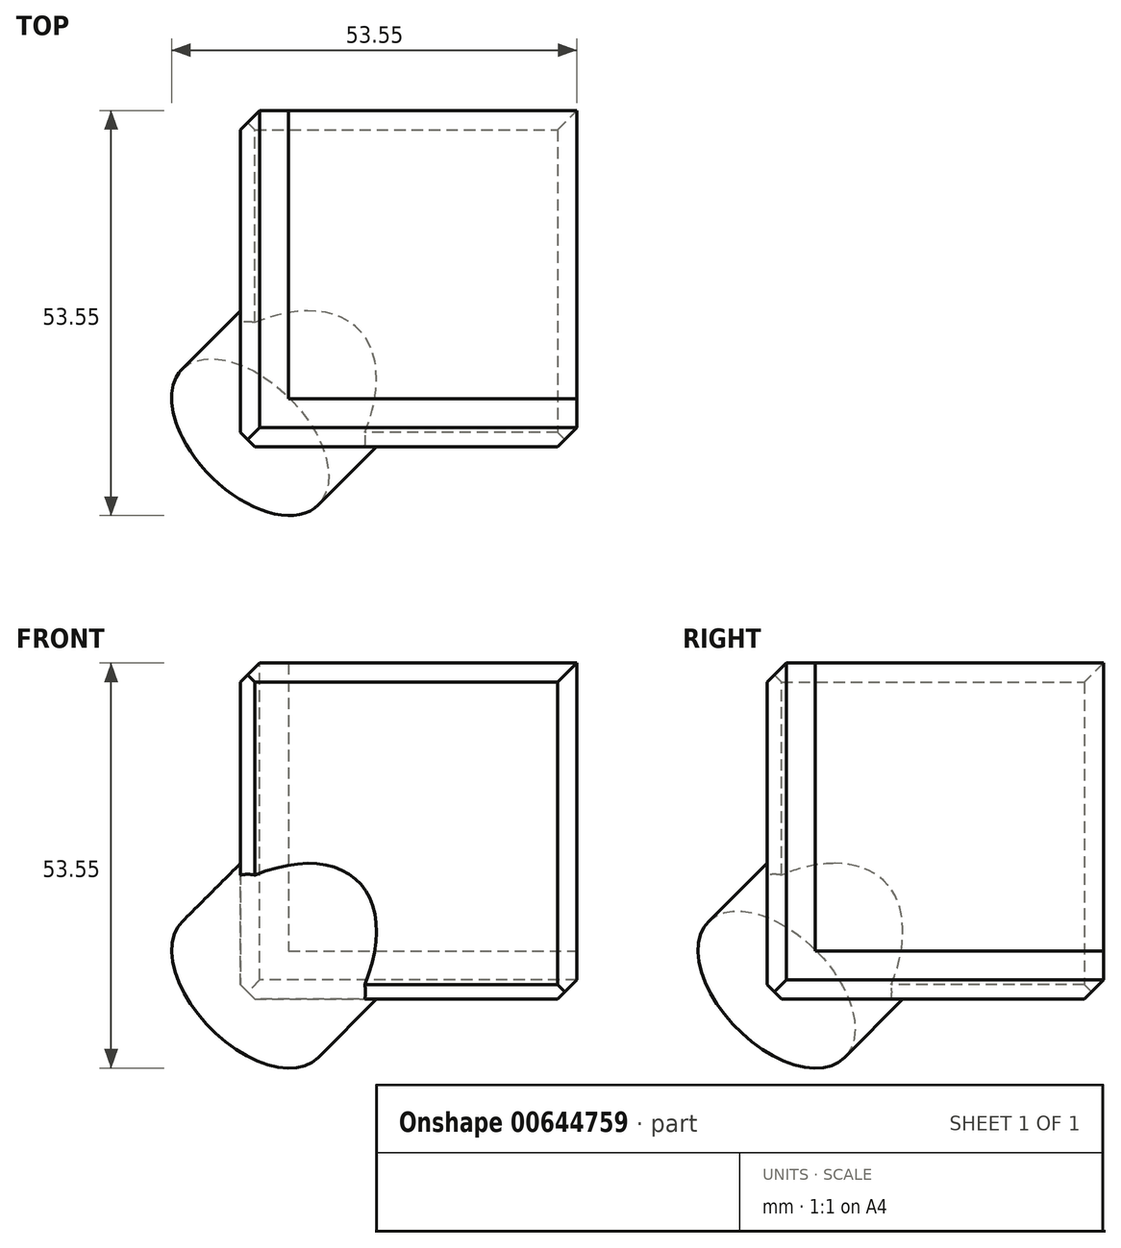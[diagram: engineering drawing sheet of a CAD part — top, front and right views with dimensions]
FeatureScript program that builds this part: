
annotation { "Feature Type Name" : "Feature", "Feature Type Description" : "" }
export const myFeature = defineFeature(function(context is Context, id is Id, definition is map)
    precondition{}
    {
        {
            var Q0;
            Q0=qCreatedBy(makeId("Top.planeOp"),FACE);
            var sketch = newSketch(context, id + "F0", { "sketchPlane" : qUnion([Q0])});
            skLineSegment(sketch, "E0.bottom", {"start": v(-20.24, 21.46) * mm, "end": v(24.2, 21.46) * mm});
            skLineSegment(sketch, "E0.top", {"start": v(-20.24, -22.99) * mm, "end": v(24.2, -22.99) * mm});
            skLineSegment(sketch, "E0.left", {"start": v(-20.24, 21.46) * mm, "end": v(-20.24, -22.99) * mm});
            skLineSegment(sketch, "E0.right", {"start": v(24.2, 21.46) * mm, "end": v(24.2, -22.99) * mm});
            skSolve(sketch);
        }
        {
            var Q0;
            Q0 = qSketchRegion(id + "F0", true);
            extrude(context, id + "F1", {"entities" : qUnion([Q0]), "depth" : 44.45 * mm, "offsetDistance" : 25.4 * mm});
        }
        {
            var Q0;
            Q0=makeQuery(id+"F1.opExtrude","SWEPT_EDGE",EDGE,{"disambiguationData":[OSD([sQuery(id+"F0.wireOp",EDGE,"E0.top"),sQuery(id+"F0.wireOp",EDGE,"E0.left")])]});
            var Q1;
            Q1=makeQuery(id+"F1.opExtrude","CAP_EDGE",EDGE,{"disambiguationData":[OSD([sQuery(id+"F0.wireOp",EDGE,"E0.top")])],"isStart":true});
            var Q2;
            Q2=makeQuery(id+"F1.opExtrude","CAP_EDGE",EDGE,{"disambiguationData":[OSD([sQuery(id+"F0.wireOp",EDGE,"E0.left")])],"isStart":true});
            chamfer(context, id + "F2", {"entities" : qUnion([Q0, Q1, Q2]), "width" : 1.9 * mm, "tangentPropagation" : true});
        }
        {
            var Q0;
            {var subQ0=sQuery(id+"F0.wireOp",EDGE,"E0.left");var subQ1=sQuery(id+"F0.wireOp",EDGE,"E0.top");Q0=makeQuery(id+"F2.opChamfer","BLEND_FACE",FACE,{"disambiguationData":[OSD([subQ1,subQ0]),TDD([makeQuery(id+"F1.opExtrude","CAP_VERTEX",VERTEX,{"disambiguationData":[OSD([subQ1,subQ0])],"isStart":true})])]});}
            var sketch = newSketch(context, id + "F3", { "sketchPlane" : qUnion([Q0])});
            skLineSegment(sketch, "E1", {"start": v(-7.53, 16.93) * mm, "end": v(-6.36, 14.9) * mm});
            skLineSegment(sketch, "E2", {"start": v(-6.36, 14.9) * mm, "end": v(-7.53, 15.58) * mm, "construction": true});
            skLineSegment(sketch, "E3", {"start": v(-7.53, 15.58) * mm, "end": v(-6.36, 17.6) * mm});
            skLineSegment(sketch, "E4", {"start": v(-6.36, 17.6) * mm, "end": v(-8.7, 16.26) * mm, "construction": true});
            skLineSegment(sketch, "E5", {"start": v(-8.7, 16.26) * mm, "end": v(-6.36, 16.26) * mm});
            skPoint(sketch, "E6", {"position": v(-7.14, 16.26) * mm});
            skCircle(sketch, "E7", {"center": v(-7.14, 16.26) * mm, "radius": 12.7 * mm});
            skSolve(sketch);
        }
        {
            var Q0;
            Q0=makeQuery(id+"F3.imprint","IMPRINT",FACE,{"disambiguationData":[TD([[makeQuery(id+"F3.imprint","IMPRINT",EDGE,{"derivedFrom":sQuery(id+"F3.wireOp",EDGE,"E7")}),1.0]])]});
            var Q1;
            {var subQ0=sQuery(id+"F3.wireOp",EDGE,"E1");var subQ6=sQuery(id+"F3.wireOp",EDGE,"E5");var subQ7=makeQuery(id+"F3.imprint","INTERSECT",VERTEX,{"derivedFrom":[subQ0,sQuery(id+"F3.wireOp",EDGE,"E3"),subQ6]});Q1=makeQuery(id+"F3.imprint","IMPRINT",FACE,{"disambiguationData":[TD([[makeQuery(id+"F3.imprint","IMPRINT",EDGE,{"disambiguationData":[TD([[subQ7,1.0]])],"derivedFrom":subQ0}),-1.0]])]});}
            var Q2;
            {var subQ0=sQuery(id+"F3.wireOp",EDGE,"E3");var subQ6=sQuery(id+"F3.wireOp",EDGE,"E5");var subQ7=makeQuery(id+"F3.imprint","INTERSECT",VERTEX,{"derivedFrom":[sQuery(id+"F3.wireOp",EDGE,"E1"),subQ0,subQ6]});Q2=makeQuery(id+"F3.imprint","IMPRINT",FACE,{"disambiguationData":[TD([[makeQuery(id+"F3.imprint","IMPRINT",EDGE,{"disambiguationData":[TD([[subQ7,1.0]])],"derivedFrom":subQ0}),1.0]])]});}
            var Q3;
            {var subQ0=sQuery(id+"F3.wireOp",EDGE,"E1");var subQ6=sQuery(id+"F3.wireOp",EDGE,"E3");var subQ7=makeQuery(id+"F3.imprint","INTERSECT",VERTEX,{"derivedFrom":[subQ0,subQ6,sQuery(id+"F3.wireOp",EDGE,"E5")]});Q3=makeQuery(id+"F3.imprint","IMPRINT",FACE,{"disambiguationData":[TD([[makeQuery(id+"F3.imprint","IMPRINT",EDGE,{"disambiguationData":[TD([[subQ7,1.0]])],"derivedFrom":subQ6}),-1.0]])]});}
            var Q4;
            {var subQ0=sQuery(id+"F3.wireOp",EDGE,"E1");var subQ6=sQuery(id+"F3.wireOp",EDGE,"E5");var subQ7=makeQuery(id+"F3.imprint","INTERSECT",VERTEX,{"derivedFrom":[subQ0,sQuery(id+"F3.wireOp",EDGE,"E3"),subQ6]});Q4=makeQuery(id+"F3.imprint","IMPRINT",FACE,{"disambiguationData":[TD([[makeQuery(id+"F3.imprint","IMPRINT",EDGE,{"disambiguationData":[TD([[subQ7,-1.0]])],"derivedFrom":subQ6}),-1.0]])]});}
            var Q5;
            {var subQ0=sQuery(id+"F3.wireOp",EDGE,"E3");var subQ6=sQuery(id+"F3.wireOp",EDGE,"E5");var subQ7=makeQuery(id+"F3.imprint","INTERSECT",VERTEX,{"derivedFrom":[sQuery(id+"F3.wireOp",EDGE,"E1"),subQ0,subQ6]});Q5=makeQuery(id+"F3.imprint","IMPRINT",FACE,{"disambiguationData":[TD([[makeQuery(id+"F3.imprint","IMPRINT",EDGE,{"disambiguationData":[TD([[subQ7,-1.0]])],"derivedFrom":subQ6}),1.0]])]});}
            var Q6;
            {var subQ0=sQuery(id+"F3.wireOp",EDGE,"E1");var subQ6=sQuery(id+"F3.wireOp",EDGE,"E3");var subQ7=makeQuery(id+"F3.imprint","INTERSECT",VERTEX,{"derivedFrom":[subQ0,subQ6,sQuery(id+"F3.wireOp",EDGE,"E5")]});Q6=makeQuery(id+"F3.imprint","IMPRINT",FACE,{"disambiguationData":[TD([[makeQuery(id+"F3.imprint","IMPRINT",EDGE,{"disambiguationData":[TD([[subQ7,1.0]])],"derivedFrom":subQ0}),1.0]])]});}
            var Q7;
            Q7=makeQuery(id+"F1.opExtrude","CAP_FACE",FACE,{"disambiguationData":[OSD([sQuery(id+"F0.wireOp",EDGE,"E0.bottom"),sQuery(id+"F0.wireOp",EDGE,"E0.top"),sQuery(id+"F0.wireOp",EDGE,"E0.left"),sQuery(id+"F0.wireOp",EDGE,"E0.right")])],"isStart":true});
            extrude(context, id + "F4", {"entities" : qUnion([Q0, Q1, Q2, Q3, Q4, Q5, Q6]), "operationType" : NewBodyOperationType.ADD, "oppositeDirection" : true, "depth" : 25.4 * mm, "endBoundEntityFace" : qUnion([Q7]), "offsetDistance" : 25.4 * mm});
        }
        {
            var Q0;
            Q0=makeQuery(id+"F1.opExtrude","SWEPT_FACE",FACE,{"disambiguationData":[OSD([sQuery(id+"F0.wireOp",EDGE,"E0.right")])]});
            var sketch = newSketch(context, id + "F5", { "sketchPlane" : qUnion([Q0])});
            skLineSegment(sketch, "E8.bottom", {"start": v(21.46, 44.45) * mm, "end": v(-16.64, 44.45) * mm});
            skLineSegment(sketch, "E8.top", {"start": v(21.46, 6.35) * mm, "end": v(-16.64, 6.35) * mm});
            skLineSegment(sketch, "E8.left", {"start": v(21.46, 44.45) * mm, "end": v(21.46, 6.35) * mm});
            skLineSegment(sketch, "E8.right", {"start": v(-16.64, 44.45) * mm, "end": v(-16.64, 6.35) * mm});
            skSolve(sketch);
        }
        {
            var Q0;
            Q0=makeQuery(id+"F5.imprint","IMPRINT",FACE,{"disambiguationData":[TD([[makeQuery(id+"F5.imprint","IMPRINT",EDGE,{"derivedFrom":sQuery(id+"F5.wireOp",EDGE,"E8.bottom")}),1.0]])]});
            extrude(context, id + "F6", {"entities" : qUnion([Q0]), "operationType" : NewBodyOperationType.REMOVE, "oppositeDirection" : true, "depth" : 38.1 * mm, "offsetDistance" : 25.4 * mm});
        }
        {
            var Q0;
            Q0=makeQuery(id+"F1.opExtrude","SWEPT_EDGE",EDGE,{"disambiguationData":[OSD([sQuery(id+"F0.wireOp",EDGE,"E0.bottom"),sQuery(id+"F0.wireOp",EDGE,"E0.left")])]});
            var Q1;
            Q1=makeQuery(id+"F1.opExtrude","CAP_EDGE",EDGE,{"disambiguationData":[OSD([sQuery(id+"F0.wireOp",EDGE,"E0.bottom")])],"isStart":true});
            var Q2;
            Q2=makeQuery(id+"F1.opExtrude","CAP_EDGE",EDGE,{"disambiguationData":[OSD([sQuery(id+"F0.wireOp",EDGE,"E0.top")])],"isStart":false});
            var Q3;
            Q3=makeQuery(id+"F1.opExtrude","CAP_EDGE",EDGE,{"disambiguationData":[OSD([sQuery(id+"F0.wireOp",EDGE,"E0.left")])],"isStart":false});
            var Q4;
            Q4=makeQuery(id+"F1.opExtrude","SWEPT_EDGE",EDGE,{"disambiguationData":[OSD([sQuery(id+"F0.wireOp",EDGE,"E0.top"),sQuery(id+"F0.wireOp",EDGE,"E0.right")])]});
            var Q5;
            Q5=makeQuery(id+"F1.opExtrude","CAP_EDGE",EDGE,{"disambiguationData":[OSD([sQuery(id+"F0.wireOp",EDGE,"E0.right")])],"isStart":true});
            var Q6;
            Q6=makeQuery(id+"F6.boolean.opBoolean","COPY",EDGE,{"derivedFrom":makeQuery(id+"F6.opExtrude","SWEPT_EDGE",EDGE,{"disambiguationData":[OSD([sQuery(id+"F0.wireOp",EDGE,"E0.bottom"),sQuery(id+"F0.wireOp",EDGE,"E0.right"),sQuery(id+"F5.wireOp",EDGE,"E8.top"),sQuery(id+"F5.wireOp",EDGE,"E8.left")])]})});
            var Q7;
            Q7=makeQuery(id+"F6.boolean.opBoolean","COPY",EDGE,{"derivedFrom":makeQuery(id+"F6.opExtrude","CAP_EDGE",EDGE,{"disambiguationData":[OSD([sQuery(id+"F5.wireOp",EDGE,"E8.top")])],"isStart":true})});
            var Q8;
            Q8=makeQuery(id+"F6.boolean.opBoolean","COPY",EDGE,{"derivedFrom":makeQuery(id+"F6.opExtrude","CAP_EDGE",EDGE,{"disambiguationData":[OSD([sQuery(id+"F5.wireOp",EDGE,"E8.right")])],"isStart":true})});
            var Q9;
            Q9=makeQuery(id+"F6.boolean.opBoolean","COPY",EDGE,{"derivedFrom":makeQuery(id+"F6.opExtrude","SWEPT_EDGE",EDGE,{"disambiguationData":[OSD([sQuery(id+"F0.wireOp",EDGE,"E0.right"),sQuery(id+"F5.wireOp",EDGE,"E8.bottom"),sQuery(id+"F5.wireOp",EDGE,"E8.right")])]})});
            var Q10;
            Q10=makeQuery(id+"F6.boolean.opBoolean","COPY",EDGE,{"derivedFrom":makeQuery(id+"F6.opExtrude","CAP_EDGE",EDGE,{"disambiguationData":[OSD([sQuery(id+"F5.wireOp",EDGE,"E8.bottom")])],"isStart":false})});
            var Q11;
            Q11=makeQuery(id+"F6.boolean.opBoolean","COPY",EDGE,{"derivedFrom":makeQuery(id+"F6.opExtrude","CAP_EDGE",EDGE,{"disambiguationData":[OSD([sQuery(id+"F5.wireOp",EDGE,"E8.left")])],"isStart":false})});
            chamfer(context, id + "F7", {"entities" : qUnion([Q0, Q1, Q2, Q3, Q4, Q5, Q6, Q7, Q8, Q9, Q10, Q11]), "width" : 2.54 * mm, "tangentPropagation" : true});
        }
    });
